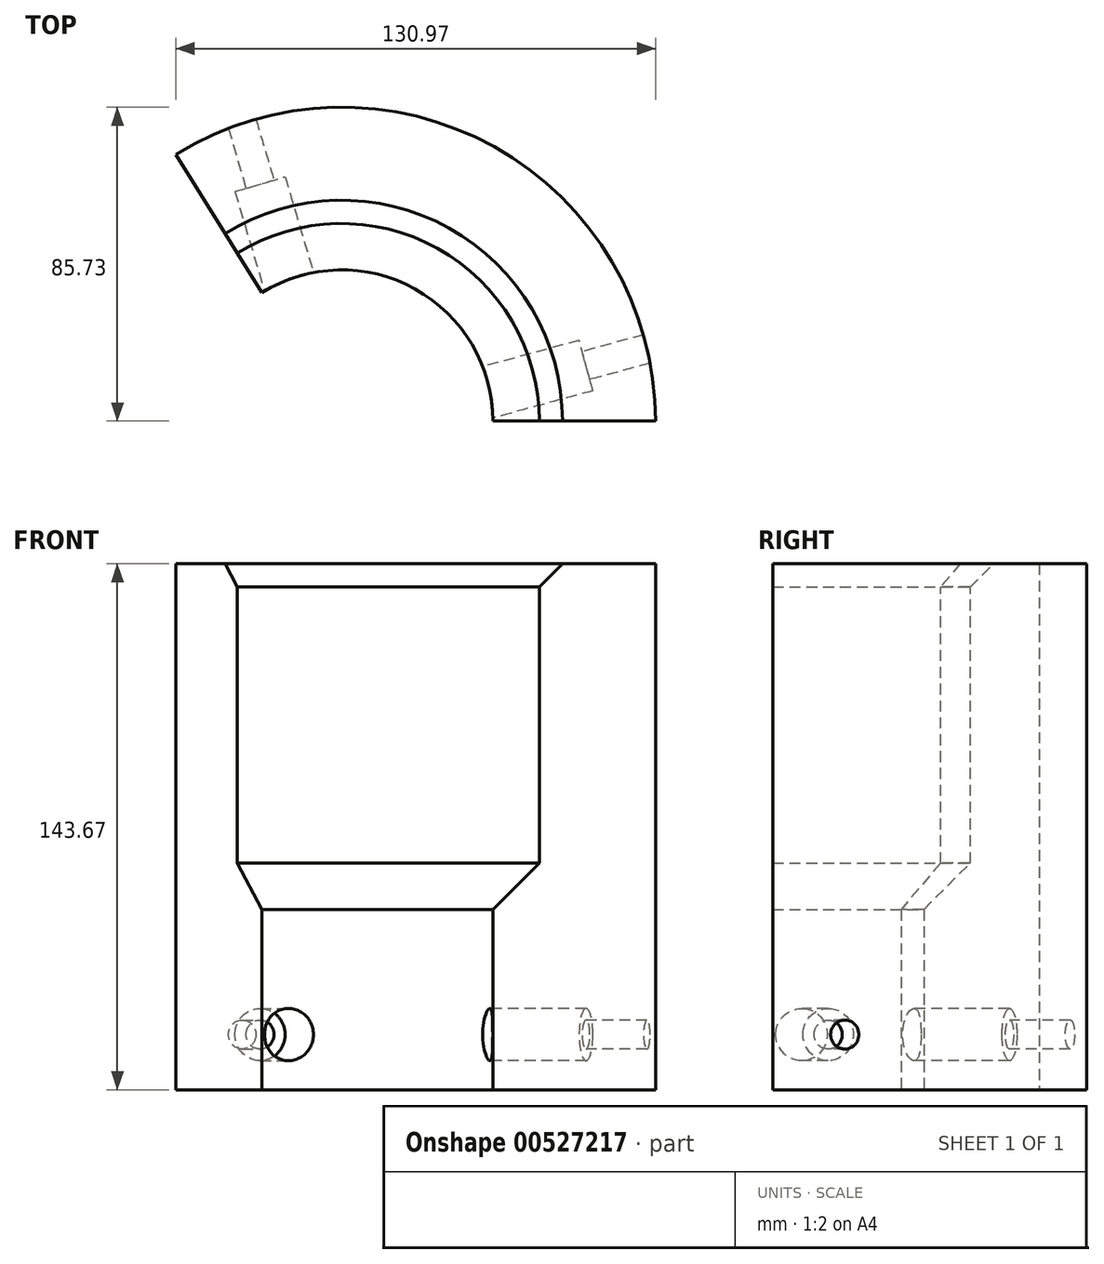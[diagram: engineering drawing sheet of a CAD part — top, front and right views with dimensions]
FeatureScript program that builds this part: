
annotation { "Feature Type Name" : "Feature", "Feature Type Description" : "" }
export const myFeature = defineFeature(function(context is Context, id is Id, definition is map)
    precondition{}
    {
        {
            var Q0;
            Q0=qCreatedBy(makeId("Top.planeOp"),FACE);
            var sketch = newSketch(context, id + "F0", { "sketchPlane" : qUnion([Q0])});
            skArc(sketch, "E0", {"start": v(41.28, 0) * mm, "mid": v(20.06, 36.07) * mm, "end": v(-21.78, 35.06) * mm});
            skArc(sketch, "E1", {"start": v(85.73, 0) * mm, "mid": v(41.65, 74.92) * mm, "end": v(-45.24, 72.81) * mm});
            skLineSegment(sketch, "E2", {"start": v(41.28, 0) * mm, "end": v(85.73, 0) * mm});
            skLineSegment(sketch, "E3", {"start": v(-21.78, 35.06) * mm, "end": v(-45.24, 72.81) * mm});
            skSolve(sketch);
        }
        {
            var Q0;
            Q0 = qSketchRegion(id + "F0", true);
            extrude(context, id + "F1", {"entities" : qUnion([Q0]), "depth" : 143.67 * mm, "offsetDistance" : 25.4 * mm});
        }
        {
            var Q0;
            Q0=makeQuery(id+"F1.opExtrude","SWEPT_FACE",FACE,{"disambiguationData":[OSD([sQuery(id+"F0.wireOp",EDGE,"E3")])]});
            var sketch = newSketch(context, id + "F2", { "sketchPlane" : qUnion([Q0])});
            skLineSegment(sketch, "E4", {"start": v(-41.27, 49.21) * mm, "end": v(-53.98, 61.91) * mm});
            skLineSegment(sketch, "E5", {"start": v(-53.98, 61.91) * mm, "end": v(-53.98, 137.32) * mm});
            skLineSegment(sketch, "E6", {"start": v(-53.97, 137.32) * mm, "end": v(-60.32, 143.67) * mm});
            skLineSegment(sketch, "E7", {"start": v(-60.33, 143.67) * mm, "end": v(-41.28, 143.67) * mm});
            skLineSegment(sketch, "E8", {"start": v(-41.28, 143.67) * mm, "end": v(-41.28, 49.21) * mm});
            skSolve(sketch);
        }
        {
            var Q0;
            Q0=qCreatedBy(makeId("Right.planeOp"),FACE);
            var sketch = newSketch(context, id + "F3", { "sketchPlane" : qUnion([Q0])});
            skLineSegment(sketch, "E9", {"start": v(0, 0) * mm, "end": v(0, 91.38) * mm});
            skSolve(sketch);
        }
        {
            var Q0;
            Q0 = qSketchRegion(id + "F2", true);
            var Q1;
            Q1=sQuery(id+"F3.wireOp",EDGE,"E9");
            revolve(context, id + "F4", {"operationType" : NewBodyOperationType.REMOVE, "entities" : qUnion([Q0]), "axis" : qUnion([Q1]), "revolveType" : RevolveType.FULL, "oppositeDirection" : true});
        }
        {
            var Q0;
            Q0=makeQuery(id+"F1.opExtrude","SWEPT_EDGE",EDGE,{"disambiguationData":[OSD([sQuery(id+"F0.wireOp",EDGE,"E0"),sQuery(id+"F0.wireOp",EDGE,"E3")])]});
            cPlane(context, id + "F5", {"entities" : qUnion([Q0]), "cplaneType" : CPlaneType.LINE_ANGLE, "offset" : 25.4 * mm, "angle" : 73.5 * degree, "width" : 152.4 * mm, "height" : 152.4 * mm});
        }
        {
            var Q0;
            Q0=qCreatedBy(id+"F5.planeOp",FACE);
            var sketch = newSketch(context, id + "F6", { "sketchPlane" : qUnion([Q0])});
            skCircle(sketch, "E10", {"center": v(3, 15.08) * mm, "radius": 7.14 * mm});
            skSolve(sketch);
        }
        {
            var Q0;
            Q0=qCreatedBy(id+"F5.planeOp",FACE);
            var sketch = newSketch(context, id + "F7", { "sketchPlane" : qUnion([Q0])});
            skCircle(sketch, "E11", {"center": v(3, 15.08) * mm, "radius": 3.97 * mm});
            skSolve(sketch);
        }
        {
            var Q0;
            Q0 = qSketchRegion(id + "F7", true);
            extrude(context, id + "F8", {"entities" : qUnion([Q0]), "operationType" : NewBodyOperationType.REMOVE, "depth" : 76.2 * mm, "offsetDistance" : 25.4 * mm});
        }
        {
            var Q0;
            Q0 = qSketchRegion(id + "F6", true);
            extrude(context, id + "F9", {"entities" : qUnion([Q0]), "operationType" : NewBodyOperationType.REMOVE, "depth" : 28.57 * mm, "offsetDistance" : 25.4 * mm});
        }
        {
            var Q0;
            Q0=makeQuery(id+"F1.opExtrude","SWEPT_EDGE",EDGE,{"disambiguationData":[OSD([sQuery(id+"F0.wireOp",EDGE,"E0"),sQuery(id+"F0.wireOp",EDGE,"E2")])]});
            cPlane(context, id + "F10", {"entities" : qUnion([Q0]), "cplaneType" : CPlaneType.LINE_ANGLE, "offset" : 25.4 * mm, "angle" : 15.25 * degree, "oppositeDirection" : true, "width" : 152.4 * mm, "height" : 152.4 * mm});
        }
        {
            var Q0;
            Q0=qCreatedBy(id+"F10.planeOp",FACE);
            var sketch = newSketch(context, id + "F11", { "sketchPlane" : qUnion([Q0])});
            skCircle(sketch, "E12", {"center": v(2.92, 15.08) * mm, "radius": 7.14 * mm});
            skSolve(sketch);
        }
        {
            var Q0;
            Q0=qCreatedBy(id+"F10.planeOp",FACE);
            var sketch = newSketch(context, id + "F12", { "sketchPlane" : qUnion([Q0])});
            skCircle(sketch, "E13", {"center": v(2.92, 15.08) * mm, "radius": 3.97 * mm});
            skSolve(sketch);
        }
        {
            var Q0;
            Q0 = qSketchRegion(id + "F11", true);
            extrude(context, id + "F13", {"entities" : qUnion([Q0]), "operationType" : NewBodyOperationType.REMOVE, "oppositeDirection" : true, "depth" : 28.57 * mm, "offsetDistance" : 25.4 * mm});
        }
        {
            var Q0;
            Q0 = qSketchRegion(id + "F12", true);
            extrude(context, id + "F14", {"entities" : qUnion([Q0]), "operationType" : NewBodyOperationType.REMOVE, "oppositeDirection" : true, "depth" : 76.2 * mm, "offsetDistance" : 25.4 * mm});
        }
    });
